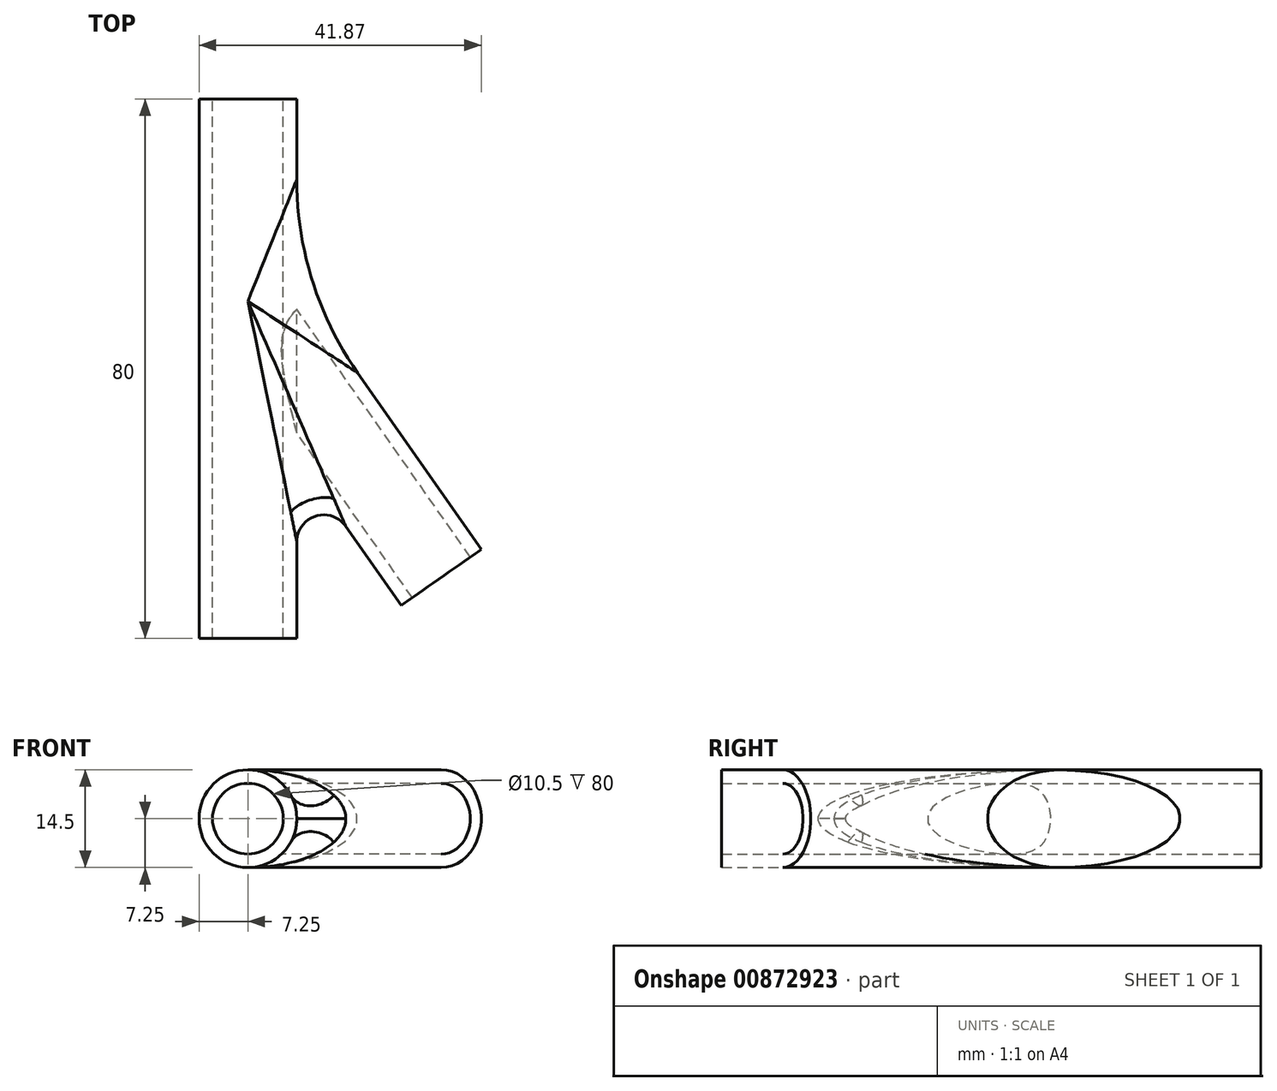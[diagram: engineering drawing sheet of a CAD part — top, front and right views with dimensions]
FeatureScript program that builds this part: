
annotation { "Feature Type Name" : "Feature", "Feature Type Description" : "" }
export const myFeature = defineFeature(function(context is Context, id is Id, definition is map)
    precondition{}
    {
        {
            assignVariable(context, id + "F0", {"name" : "angle", "anyValue" : 35});
        }
        {
            var Q0;
            Q0=qCreatedBy(makeId("Top.planeOp"),FACE);
            var sketch = newSketch(context, id + "F1", { "sketchPlane" : qUnion([Q0])});
            skCircle(sketch, "E0", {"center": v(0, 0) * mm, "radius": 77.94 * mm, "construction": true});
            skSolve(sketch);
        }
        {
            var Q0;
            Q0=qCreatedBy(makeId("Front.planeOp"),FACE);
            var sketch = newSketch(context, id + "F2", { "sketchPlane" : qUnion([Q0])});
            skCircle(sketch, "E1", {"center": v(0, 0) * mm, "radius": 7.25 * mm});
            skCircle(sketch, "E2", {"center": v(0, 0) * mm, "radius": 5.25 * mm});
            skSolve(sketch);
        }
        {
            var Q0;
            Q0=qSketchRegion(id+"F2",true);
            extrude(context, id + "F3", {"entities" : qUnion([Q0]), "depth" : 50 * mm, "offsetDistance" : 25 * mm});
        }
        {
            var Q0;
            Q0=makeQuery(id+"F3.opExtrude","SWEPT_BODY",BODY,{"disambiguationData":[OSD([sQuery(id+"F2.wireOp",EDGE,"E1"),sQuery(id+"F2.wireOp",EDGE,"E2")])]});
            var Q1;
            Q1=sQuery(id+"F1.wireOp",EDGE,"E0");
            circularPattern(context, id + "F4", {"operationType" : NewBodyOperationType.ADD, "entities" : qUnion([Q0]), "axis" : qUnion([Q1]), "angle" : (getVariable(context, 'angle')) * degree, "instanceCount" : 2, "equalSpace" : true});
        }
        {
            var Q0;
            Q0 = qSketchRegion(id + "F2", true);
            extrude(context, id + "F5", {"entities" : qUnion([Q0]), "operationType" : NewBodyOperationType.ADD, "oppositeDirection" : true, "depth" : 30 * mm, "offsetDistance" : 25 * mm});
        }
        {
            var Q0;
            Q0=makeQuery(id+"F2.imprint","IMPRINT",FACE,{"disambiguationData":[TD([[makeQuery(id+"F2.imprint","IMPRINT",EDGE,{"derivedFrom":sQuery(id+"F2.wireOp",EDGE,"E2")}),1.0]])]});
            extrude(context, id + "F6", {"entities" : qUnion([Q0]), "operationType" : NewBodyOperationType.REMOVE, "endBound" : BoundingType.THROUGH_ALL, "depth" : 25 * mm, "offsetDistance" : 25 * mm});
        }
        {
            var Q0;
            Q0=makeQuery(id+"F2.imprint","IMPRINT",FACE,{"disambiguationData":[TD([[makeQuery(id+"F2.imprint","IMPRINT",EDGE,{"derivedFrom":sQuery(id+"F2.wireOp",EDGE,"E2")}),1.0]])]});
            extrude(context, id + "F7", {"entities" : qUnion([Q0]), "operationType" : NewBodyOperationType.REMOVE, "endBound" : BoundingType.THROUGH_ALL, "oppositeDirection" : true, "depth" : 25 * mm, "offsetDistance" : 25 * mm});
        }
        {
            var Q0;
            {var subQ0=makeQuery(id+"F3.opExtrude","SWEPT_FACE",FACE,{"disambiguationData":[OSD([sQuery(id+"F2.wireOp",EDGE,"E1")])]});Q0=makeQuery(id+"F4.boolean.opBoolean","INTERSECT",EDGE,{"derivedFrom":[subQ0,makeQuery(id+"F4.opPattern","COPY",FACE,{"derivedFrom":subQ0,"instanceName":"1"})]});}
            fillet(context, id + "F8", {"entities" : qUnion([Q0]), "radius" : 4 * mm, "tangentPropagation" : true, "allowEdgeOverflow" : false});
        }
        {
            var Q0;
            {var subQ0=sQuery(id+"F2.wireOp",EDGE,"E1");var subQ1=makeQuery(id+"F3.opExtrude","SWEPT_FACE",FACE,{"disambiguationData":[OSD([subQ0])]});Q0=makeQuery(id+"F5.boolean.opBoolean","INTERSECT",EDGE,{"derivedFrom":[makeQuery(id+"F4.boolean.opBoolean","SPLIT",FACE,{"disambiguationData":[TD([subQ1])],"derivedFrom":makeQuery(id+"F4.opPattern","COPY",FACE,{"derivedFrom":subQ1,"instanceName":"1"})}),makeQuery(id+"F5.opExtrude","SWEPT_FACE",FACE,{"disambiguationData":[OSD([subQ0])]})]});}
            fillet(context, id + "F9", {"entities" : qUnion([Q0]), "radius" : 50 * mm, "tangentPropagation" : true, "allowEdgeOverflow" : false});
        }
    });
